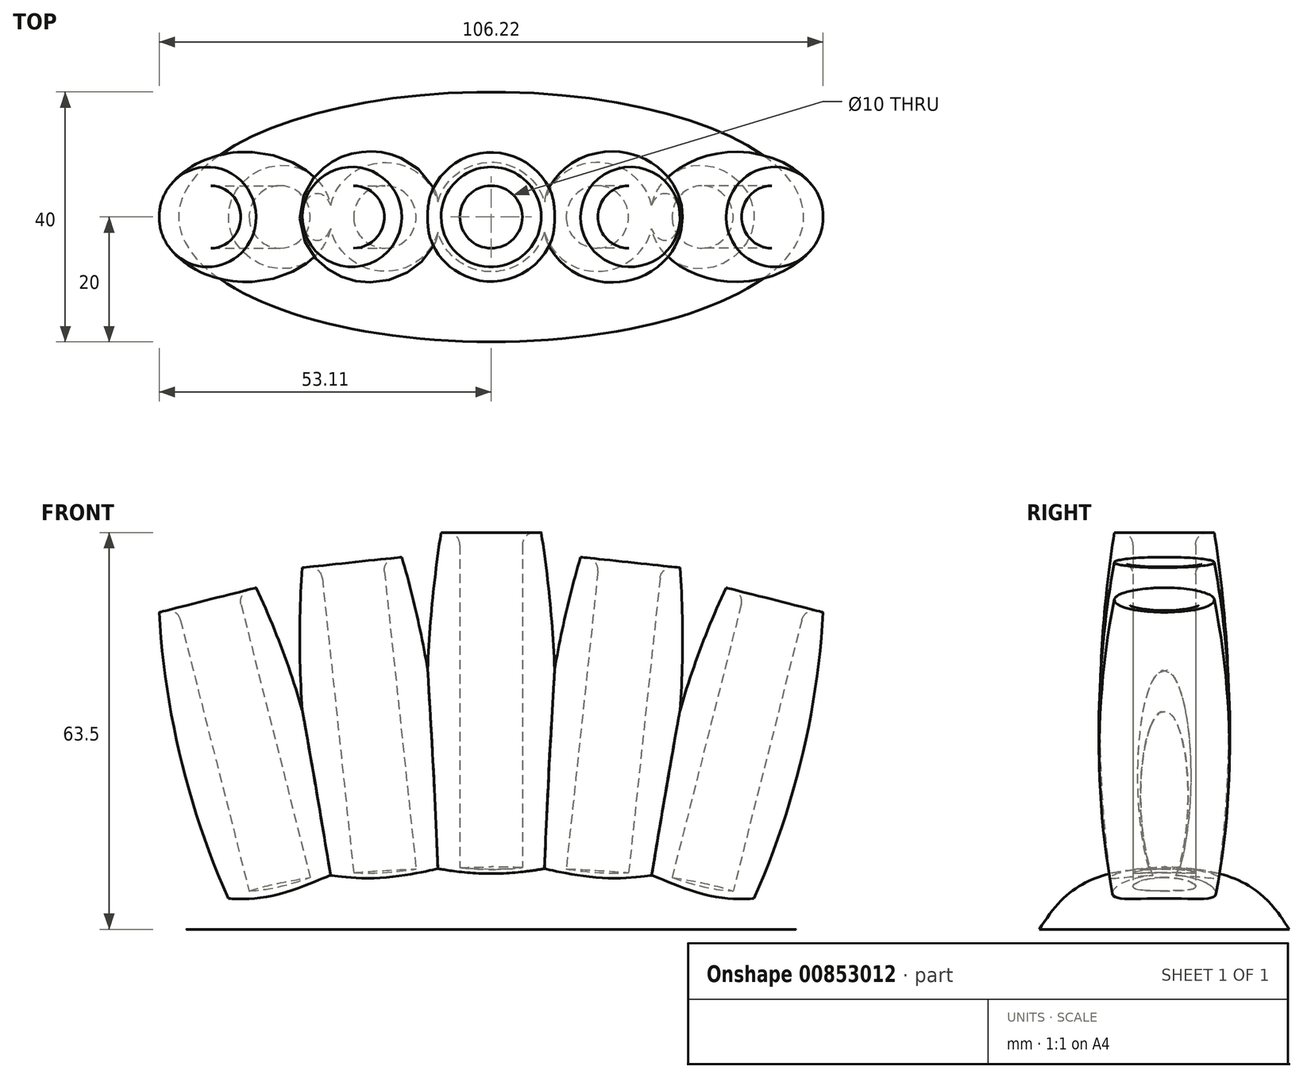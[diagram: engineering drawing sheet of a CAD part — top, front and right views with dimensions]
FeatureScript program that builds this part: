
annotation { "Feature Type Name" : "Feature", "Feature Type Description" : "" }
export const myFeature = defineFeature(function(context is Context, id is Id, definition is map)
    precondition{}
    {
        {
            var Q0;
            Q0=qCreatedBy(makeId("Top.planeOp"),FACE);
            var sketch = newSketch(context, id + "F0", { "sketchPlane" : qUnion([Q0])});
            skEllipse(sketch, "E0", {"center": v(0, 0) * mm, "majorRadius": 50 * mm, "minorRadius": 20 * mm, "majorAxis": v(1, 0)});
            skSolve(sketch);
        }
        {
            var Q0;
            Q0=qCreatedBy(makeId("Front.planeOp"),FACE);
            var sketch = newSketch(context, id + "F1", { "sketchPlane" : qUnion([Q0])});
            skPoint(sketch, "E1", {"position": v(0, 10) * mm});
            skPoint(sketch, "E2", {"position": v(0, 3.5) * mm});
            skSolve(sketch);
        }
        {
            var Q0;
            Q0=qCreatedBy(makeId("Top.planeOp"),FACE);
            var Q1;
            Q1=sQuery(id+"F1.wireOp",VERTEX,"E2");
            cPlane(context, id + "F2", {"entities" : qUnion([Q0, Q1]), "cplaneType" : CPlaneType.PLANE_POINT, "offset" : 25 * mm, "width" : 150 * mm, "height" : 150 * mm});
        }
        {
            var Q0;
            Q0=qCreatedBy(id+"F2.planeOp",FACE);
            var sketch = newSketch(context, id + "F3", { "sketchPlane" : qUnion([Q0])});
            skEllipse(sketch, "E3", {"center": v(0, 0) * mm, "majorRadius": 45 * mm, "minorRadius": 17.5 * mm, "majorAxis": v(1, 0)});
            skSolve(sketch);
        }
        {
            var Q0;
            Q0=makeQuery(id+"F0.imprint","IMPRINT",FACE,{"disambiguationData":[TD([[makeQuery(id+"F0.imprint","IMPRINT",EDGE,{"derivedFrom":sQuery(id+"F0.wireOp",EDGE,"E0")}),1.0]])]});
            var Q1;
            Q1=makeQuery(id+"F3.imprint","IMPRINT",FACE,{"disambiguationData":[TD([[makeQuery(id+"F3.imprint","IMPRINT",EDGE,{"derivedFrom":sQuery(id+"F3.wireOp",EDGE,"E3")}),1.0]])]});
            var Q2;
            Q2=sQuery(id+"F1.wireOp",VERTEX,"E1");
            loft(context, id + "F4", {"sheetProfilesArray" : [{ "sheetProfileEntities" : qUnion([Q0]) }, { "sheetProfileEntities" : qUnion([Q1]) }, { "sheetProfileEntities" : qUnion([Q2]) }]});
        }
        {
            var Q0;
            Q0=qCreatedBy(makeId("Front.planeOp"),FACE);
            var sketch = newSketch(context, id + "F5", { "sketchPlane" : qUnion([Q0])});
            skLineSegment(sketch, "E4", {"start": v(0, 0) * mm, "end": v(0, 63.5) * mm});
            skLineSegment(sketch, "E5", {"start": v(-5, 63.5) * mm, "end": v(-5, 3.5) * mm});
            skLineSegment(sketch, "E6", {"start": v(-5, 3.5) * mm, "end": v(-8, 3.5) * mm});
            skLineSegment(sketch, "E7", {"start": v(-8, 63.5) * mm, "end": v(-5, 63.5) * mm});
            skArc(sketch, "E8", {"start": v(-8, 63.5) * mm, "mid": v(-10.33, 33.5) * mm, "end": v(-8, 3.5) * mm});
            skLineSegment(sketch, "E9", {"start": v(-16, 0) * mm, "end": v(-22.62, 62.11) * mm});
            skLineSegment(sketch, "E10", {"start": v(-32, 0) * mm, "end": v(-46.6, 57.63) * mm});
            skLineSegment(sketch, "E11", {"start": v(-27.23, 58.2) * mm, "end": v(-21.4, 3.5) * mm});
            skLineSegment(sketch, "E12", {"start": v(-21.4, 3.5) * mm, "end": v(-24.38, 3.18) * mm});
            skLineSegment(sketch, "E13", {"start": v(-27.23, 58.2) * mm, "end": v(-30.21, 57.87) * mm});
            skArc(sketch, "E14", {"start": v(-30.21, 57.87) * mm, "mid": v(-29.77, 30.26) * mm, "end": v(-24.38, 3.18) * mm});
            skLineSegment(sketch, "E15", {"start": v(-50.2, 51.47) * mm, "end": v(-37.92, 3) * mm});
            skLineSegment(sketch, "E16", {"start": v(-37.92, 3) * mm, "end": v(-40.83, 2.26) * mm});
            skLineSegment(sketch, "E17", {"start": v(-50.2, 51.47) * mm, "end": v(-53.1, 50.73) * mm});
            skArc(sketch, "E18", {"start": v(-53.1, 50.73) * mm, "mid": v(-49.3, 25.9) * mm, "end": v(-40.83, 2.26) * mm});
            skLineSegment(sketch, "E19.MirrorCS", {"start": v(16, 0) * mm, "end": v(22.62, 62.11) * mm});
            skLineSegment(sketch, "E20.MirrorCS", {"start": v(27.23, 58.2) * mm, "end": v(21.4, 3.5) * mm});
            skArc(sketch, "E21.MirrorCS", {"start": v(30.21, 57.87) * mm, "mid": v(29.77, 30.26) * mm, "end": v(24.38, 3.18) * mm});
            skLineSegment(sketch, "E22.MirrorCS", {"start": v(27.23, 58.2) * mm, "end": v(30.21, 57.87) * mm});
            skLineSegment(sketch, "E23.MirrorCS", {"start": v(21.4, 3.5) * mm, "end": v(24.38, 3.18) * mm});
            skLineSegment(sketch, "E24.MirrorCS", {"start": v(32, 0) * mm, "end": v(46.6, 57.63) * mm});
            skLineSegment(sketch, "E25.MirrorCS", {"start": v(50.2, 51.47) * mm, "end": v(37.92, 3) * mm});
            skLineSegment(sketch, "E26.MirrorCS", {"start": v(37.92, 3) * mm, "end": v(40.83, 2.26) * mm});
            skArc(sketch, "E27.MirrorCS", {"start": v(53.1, 50.73) * mm, "mid": v(49.3, 25.9) * mm, "end": v(40.83, 2.26) * mm});
            skLineSegment(sketch, "E28.MirrorCS", {"start": v(50.2, 51.47) * mm, "end": v(53.1, 50.73) * mm});
            skSolve(sketch);
        }
        {
            var Q0;
            Q0=makeQuery(id+"F5.imprint","IMPRINT",FACE,{"disambiguationData":[TD([[makeQuery(id+"F5.imprint","IMPRINT",EDGE,{"derivedFrom":sQuery(id+"F5.wireOp",EDGE,"E5")}),-1.0]])]});
            var Q1;
            Q1=sQuery(id+"F5.wireOp",EDGE,"E4");
            revolve(context, id + "F6", {"operationType" : NewBodyOperationType.ADD, "surfaceOperationType" : NewSurfaceOperationType.NEW, "entities" : qUnion([Q0]), "axis" : qUnion([Q1]), "revolveType" : RevolveType.FULL});
        }
        {
            var Q0;
            Q0=makeQuery(id+"F5.imprint","IMPRINT",FACE,{"disambiguationData":[TD([[makeQuery(id+"F5.imprint","IMPRINT",EDGE,{"derivedFrom":sQuery(id+"F5.wireOp",EDGE,"E11")}),-1.0]])]});
            var Q1;
            Q1=sQuery(id+"F5.wireOp",EDGE,"E9");
            revolve(context, id + "F7", {"operationType" : NewBodyOperationType.ADD, "surfaceOperationType" : NewSurfaceOperationType.NEW, "entities" : qUnion([Q0]), "axis" : qUnion([Q1]), "revolveType" : RevolveType.FULL});
        }
        {
            var Q0;
            Q0=makeQuery(id+"F5.imprint","IMPRINT",FACE,{"disambiguationData":[TD([[makeQuery(id+"F5.imprint","IMPRINT",EDGE,{"derivedFrom":sQuery(id+"F5.wireOp",EDGE,"E15")}),-1.0]])]});
            var Q1;
            Q1=sQuery(id+"F5.wireOp",EDGE,"E10");
            revolve(context, id + "F8", {"operationType" : NewBodyOperationType.ADD, "surfaceOperationType" : NewSurfaceOperationType.NEW, "entities" : qUnion([Q0]), "axis" : qUnion([Q1]), "revolveType" : RevolveType.FULL});
        }
        {
            var Q0;
            Q0=makeQuery(id+"F5.imprint","IMPRINT",FACE,{"disambiguationData":[TD([[makeQuery(id+"F5.imprint","IMPRINT",EDGE,{"derivedFrom":sQuery(id+"F5.wireOp",EDGE,"E20.MirrorCS")}),1.0]])]});
            var Q1;
            Q1=sQuery(id+"F5.wireOp",EDGE,"E19.MirrorCS");
            revolve(context, id + "F9", {"operationType" : NewBodyOperationType.ADD, "surfaceOperationType" : NewSurfaceOperationType.NEW, "entities" : qUnion([Q0]), "axis" : qUnion([Q1]), "revolveType" : RevolveType.FULL});
        }
        {
            var Q0;
            Q0=makeQuery(id+"F5.imprint","IMPRINT",FACE,{"disambiguationData":[TD([[makeQuery(id+"F5.imprint","IMPRINT",EDGE,{"derivedFrom":sQuery(id+"F5.wireOp",EDGE,"E25.MirrorCS")}),1.0]])]});
            var Q1;
            Q1=sQuery(id+"F5.wireOp",EDGE,"E24.MirrorCS");
            revolve(context, id + "F10", {"operationType" : NewBodyOperationType.ADD, "surfaceOperationType" : NewSurfaceOperationType.NEW, "entities" : qUnion([Q0]), "axis" : qUnion([Q1]), "revolveType" : RevolveType.FULL});
        }
        {
            var Q0;
            Q0=makeQuery(id+"F8.opRevolve","SWEPT_EDGE",EDGE,{"disambiguationData":[OSD([sQuery(id+"F5.wireOp",EDGE,"E15"),sQuery(id+"F5.wireOp",EDGE,"E17")])]});
            var Q1;
            Q1=makeQuery(id+"F7.opRevolve","SWEPT_EDGE",EDGE,{"disambiguationData":[OSD([sQuery(id+"F5.wireOp",EDGE,"E11"),sQuery(id+"F5.wireOp",EDGE,"E13")])]});
            var Q2;
            Q2=makeQuery(id+"F6.opRevolve","SWEPT_EDGE",EDGE,{"disambiguationData":[OSD([sQuery(id+"F5.wireOp",EDGE,"E5"),sQuery(id+"F5.wireOp",EDGE,"E7")])]});
            var Q3;
            Q3=makeQuery(id+"F9.opRevolve","SWEPT_EDGE",EDGE,{"disambiguationData":[OSD([sQuery(id+"F5.wireOp",EDGE,"E20.MirrorCS"),sQuery(id+"F5.wireOp",EDGE,"E22.MirrorCS")])]});
            var Q4;
            Q4=makeQuery(id+"F10.opRevolve","SWEPT_EDGE",EDGE,{"disambiguationData":[OSD([sQuery(id+"F5.wireOp",EDGE,"E25.MirrorCS"),sQuery(id+"F5.wireOp",EDGE,"E28.MirrorCS")])]});
            fillet(context, id + "F11", {"entities" : qUnion([Q0, Q1, Q2, Q3, Q4]), "radius" : 2 * mm, "tangentPropagation" : true, "allowEdgeOverflow" : false});
        }
    });
